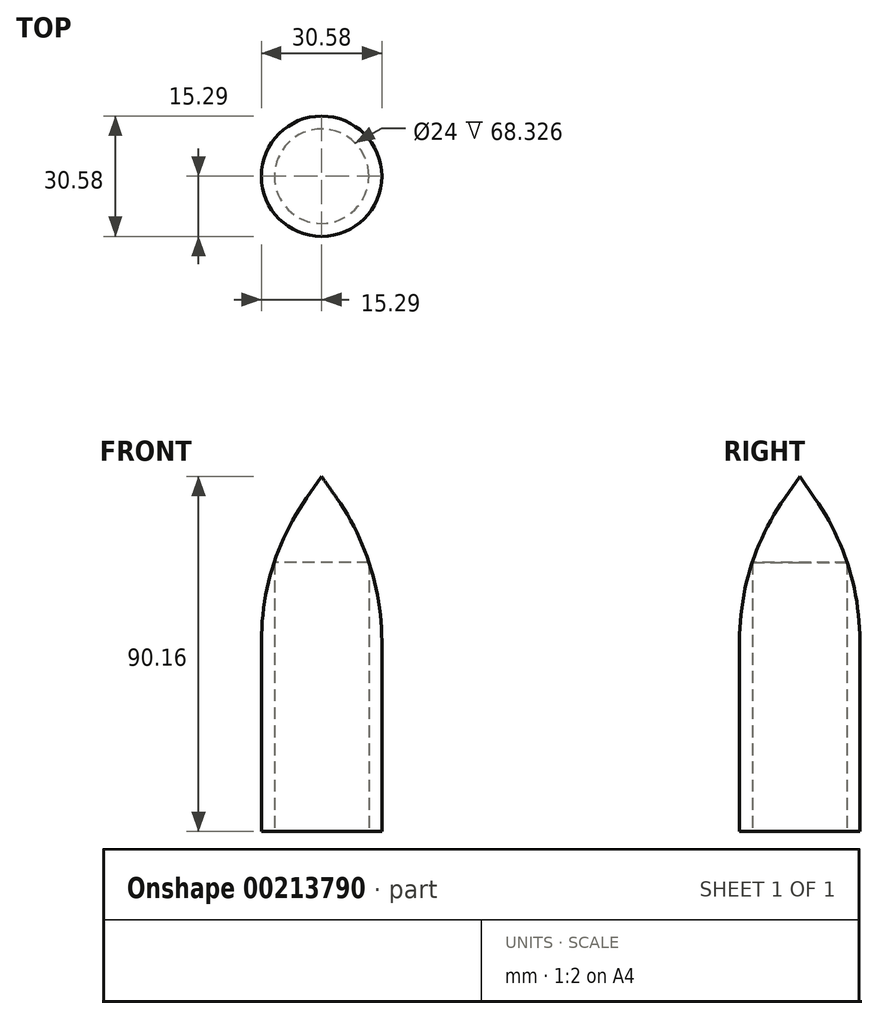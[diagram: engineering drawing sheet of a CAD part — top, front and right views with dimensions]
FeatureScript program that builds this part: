
annotation { "Feature Type Name" : "Feature", "Feature Type Description" : "" }
export const myFeature = defineFeature(function(context is Context, id is Id, definition is map)
    precondition{}
    {
        {
            var Q0;
            Q0=qCreatedBy(makeId("Top.planeOp"),FACE);
            var sketch = newSketch(context, id + "F0", { "sketchPlane" : qUnion([Q0])});
            skCircle(sketch, "E0", {"center": v(0, 0) * mm, "radius": 12 * mm});
            skCircle(sketch, "E1", {"center": v(0, 0) * mm, "radius": 15.29 * mm});
            skSolve(sketch);
        }
        {
            var Q0;
            Q0=makeQuery(id+"F0.imprint","IMPRINT",FACE,{"disambiguationData":[TD([[makeQuery(id+"F0.imprint","IMPRINT",EDGE,{"derivedFrom":sQuery(id+"F0.wireOp",EDGE,"E0")}),-1.0]])]});
            extrude(context, id + "F1", {"entities" : qUnion([Q0]), "depth" : 68.33 * mm});
        }
        {
            var Q0;
            Q0=makeQuery(id+"F1.opExtrude","CAP_FACE",FACE,{"disambiguationData":[OSD([sQuery(id+"F0.wireOp",EDGE,"E0"),sQuery(id+"F0.wireOp",EDGE,"E1")])],"isStart":false});
            var sketch = newSketch(context, id + "F2", { "sketchPlane" : qUnion([Q0])});
            skCircle(sketch, "E2.0", {"center": v(0, 0) * mm, "radius": 15.29 * mm});
            skSolve(sketch);
        }
        {
            var Q0;
            Q0 = qSketchRegion(id + "F2", true);
            extrude(context, id + "F3", {"entities" : qUnion([Q0]), "operationType" : NewBodyOperationType.ADD, "depth" : 25.4 * mm, "hasDraft" : true, "draftAngle" : 35 * degree, "draftPullDirection" : true});
        }
        {
            var Q0;
            Q0=makeQuery(id+"F3.boolean.opBoolean","MERGE",EDGE,{"derivedFrom":[makeQuery(id+"F1.opExtrude","CAP_EDGE",EDGE,{"disambiguationData":[OSD([sQuery(id+"F0.wireOp",EDGE,"E1")])],"isStart":false}),makeQuery(id+"F3.opExtrude","CAP_EDGE",EDGE,{"disambiguationData":[OSD([sQuery(id+"F2.wireOp",EDGE,"E2.0")])],"isStart":true})]});
            fillet(context, id + "F4", {"entities" : qUnion([Q0]), "radius" : 63.5 * mm, "tangentPropagation" : true, "allowEdgeOverflow" : false});
        }
    });
